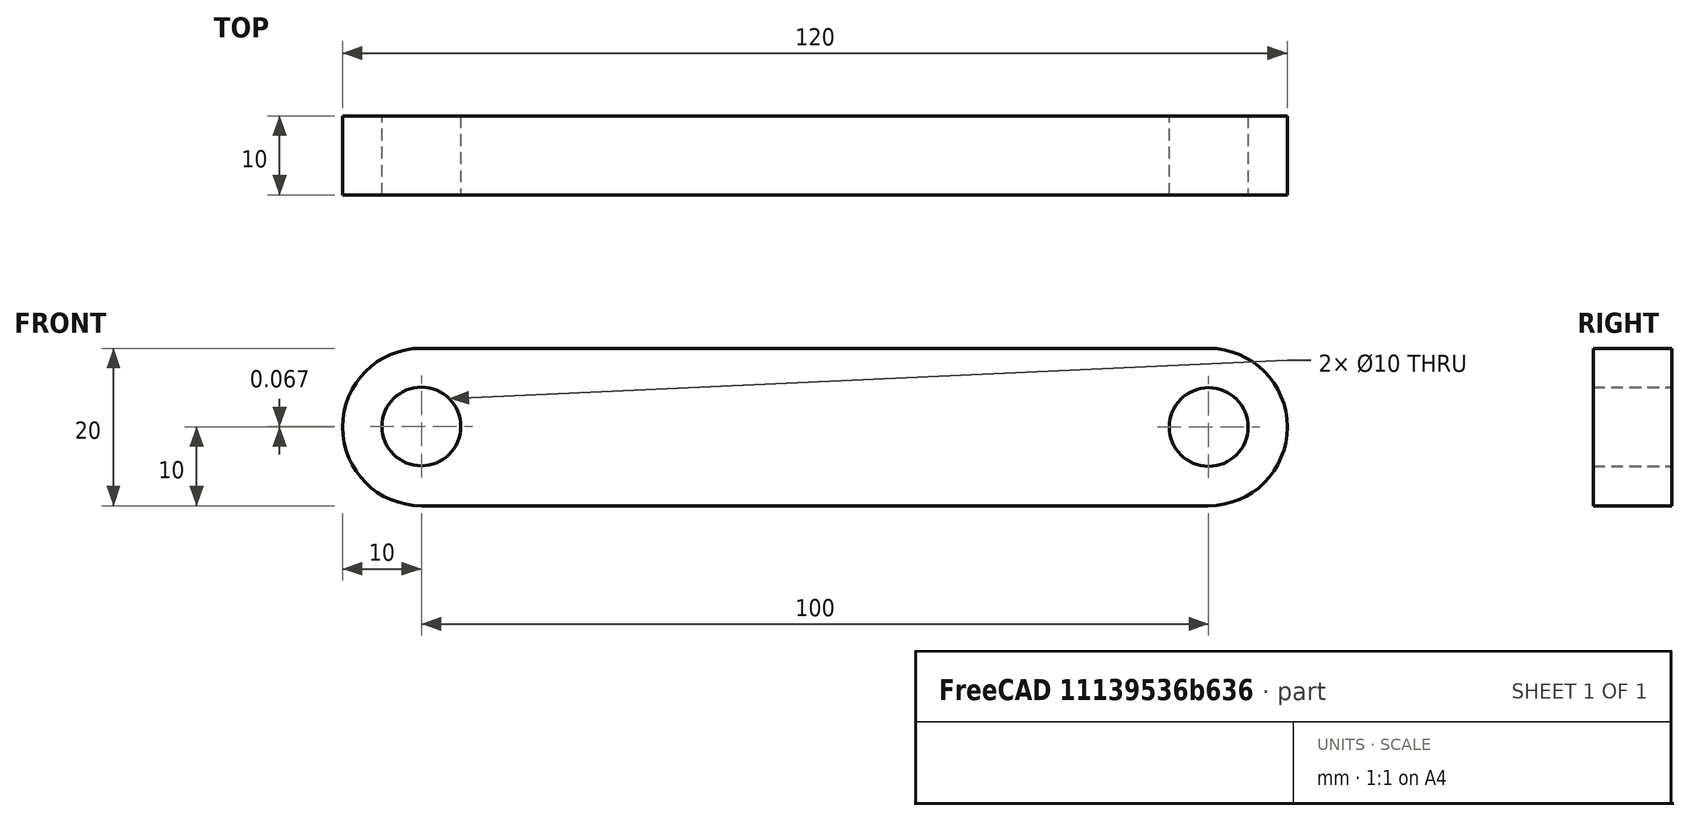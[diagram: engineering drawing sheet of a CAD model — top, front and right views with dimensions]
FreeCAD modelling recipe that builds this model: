
FCSTD DOCUMENT  (FreeCAD 0.21R33668 +26 (Git))
Label: Tuto1-001
License: All rights reserved
LicenseURL: http://en.wikipedia.org/wiki/All_rights_reserved
objects: PartDesign::CoordinateSystem×5, App::DocumentObjectGroup×3, Sketcher::SketchObject×2, App::Link×2, App::FeaturePython×1, App::Part×1, PartDesign::Pad×1, PartDesign::Body×1
note: 10 computed .brp shape members not serialized (recipe doc carries the construction recipe); baked Part::Feature solids carry a one-line shape summary decoded from their .brp

FEATURE [PartDesign::CoordinateSystem] LCS_Origin
  AttacherType = Attacher::AttachEngine3D
  MapMode = 2
  Support = -> [X_Axis]
FEATURE [App::DocumentObjectGroup] Constraints
FEATURE [App::FeaturePython] Variables  # WARN: FeaturePython — macro-defined, semantics opaque (R4)
  Type = App::PropertyContainer
  rotation_bielle1 = 79
FEATURE [App::DocumentObjectGroup] Configurations
FEATURE [Sketcher::SketchObject] Sketch_1
  FullyConstrained = true
  Support = -> [YZ_Plane]
  expr: Constraints[11] = Variables.rotation_bielle1
  sketch-geometry (3):
    g0: LineSegment StartX=90.2102 StartY=121.516 StartZ=0 EndX=1.29856 EndY=242.324 EndZ=0
    g1: LineSegment StartX=0 StartY=120 StartZ=0 EndX=19.0809 EndY=218.163 EndZ=0
    g2: LineSegment StartX=0 StartY=50 StartZ=0 EndX=72.4279 EndY=145.678 EndZ=0
  constraints (12):
    c: PointOnObject(g1,g0)
    c: PointOnObject(g2,g0)
    c: PointOnObject(g1,g-2)
    c: Distance(g1,g0) = 30
    c: Distance(g2,g0) = 30
    c: PointOnObject(g2,g-2)
    c: Distance(g2) = 120
    c: DistanceY(g-1,g1) = 120
    c: Distance(g1,g1) = 100
    c: Distance(g0) = 150
    c: DistanceY(g-1,g2) = 50
    c: Angle(g-1,g1) = 1.37881
FEATURE [PartDesign::CoordinateSystem] LCS_1
  AttacherType = Attacher::AttachEngine3D
  MapMode = 7
  Placement = pos=(0,120,0) rot=(0.990855,-0.095409,-0.095409;1.57998rad)
  Support = -> [Sketch_1]
FEATURE [PartDesign::CoordinateSystem] LCS_2
  AttacherType = Attacher::AttachEngine3D
  MapMode = 7
  Placement = pos=(90.2102,121.516,0) rot=(0.906999,0.297785,0.297785;1.66826rad)
  Support = -> [Sketch_1]
FEATURE [PartDesign::CoordinateSystem] LCS_3
  AttacherType = Attacher::AttachEngine3D
  MapMode = 7
  Placement = pos=(-3.6e-15,50,0) rot=(0.903307,-0.303345,-0.303345;1.67231rad)
  Support = -> [Sketch_1]
FEATURE [PartDesign::CoordinateSystem] LCS_0
  AttacherType = Attacher::AttachEngine3D
  MapMode = 2
  Support = -> [X_Axis001]
FEATURE [App::Link] Body001
  AttachedBy = #LCS_0
  AttachedTo = Parent Assembly#LCS_1
  AttachmentOffset = pos=(0,0,0) rot=(-0.707107,0,0.707107;3.14159rad)
  LinkPlacement = pos=(0,120,0) rot=(-0.651074,-0.536704,0.536704;1.98733rad)
  LinkedObject = -> Body
  Placement = pos=(0,120,0) rot=(-0.651074,-0.536704,0.536704;1.98733rad)
  SolverId = Asm4EE
  expr: Placement = LCS_1.Placement * AttachmentOffset * LCS_0.Placement ^ -1
FEATURE [App::Link] Body002
  AttachedBy = #LCS_0
  AttachedTo = Parent Assembly#LCS_3
  AttachmentOffset = pos=(0,0,0) rot=(-0.707107,0,0.707107;3.14159rad)
  LinkPlacement = pos=(-3.6e-15,50,0) rot=(-0.818014,-0.406727,0.406727;1.77033rad)
  LinkedObject = -> Body
  Placement = pos=(-3.6e-15,50,0) rot=(-0.818014,-0.406727,0.406727;1.77033rad)
  SolverId = Asm4EE
  expr: Placement = LCS_3.Placement * AttachmentOffset * LCS_0.Placement ^ -1
FEATURE [App::Part] Assembly
  AssemblyType = Part::Link
  Group = -> [LCS_Origin,Constraints,Variables,Configurations,Sketch_1,LCS_1,LCS_2,LCS_3,Body001,Body002]
  Origin = -> Origin
  Type = Assembly
FEATURE [Sketcher::SketchObject] Sketch
  FullyConstrained = false
  MapMode = 5
  Placement = pos=(0,0,0) rot=(1,0,0;1.5708rad)
  Support = -> [XZ_Plane001]
  sketch-geometry (6):
    g0: ArcOfCircle CenterX=0 CenterY=0 CenterZ=0 NormalX=0 NormalY=0 NormalZ=1 AngleXU=0 Radius=10 StartAngle=1.5708 EndAngle=4.71239
    g1: ArcOfCircle CenterX=100 CenterY=1.1e-15 CenterZ=0 NormalX=0 NormalY=0 NormalZ=1 AngleXU=0 Radius=10 StartAngle=4.71239 EndAngle=7.85398
    g2: LineSegment StartX=-1.8e-15 StartY=-10 StartZ=0 EndX=100 EndY=-10 EndZ=0
    g3: LineSegment StartX=100 StartY=10 StartZ=0 EndX=7.958e-13 EndY=10 EndZ=0
    g4: Circle CenterX=100 CenterY=1.1e-15 CenterZ=0 NormalX=0 NormalY=0 NormalZ=1 AngleXU=0 Radius=5
    g5: Circle CenterX=0 CenterY=0.067016 CenterZ=0 NormalX=0 NormalY=0 NormalZ=1 AngleXU=0 Radius=5
  constraints (11):
    c: Tangent(g0,g2) = -1.5708
    c: Tangent(g2,g1) = -1.5708
    c: Tangent(g1,g3) = -1.5708
    c: Tangent(g3,g0) = -1.5708
    c: Equal(g0,g1)
    c: Horizontal(g2)
    c: Coincident(g0,g-1)
    c: Coincident(g4,g1)
    c: PointOnObject(g5,g-2)
    c: Radius(g5) = 5
    c: DistanceX(g5,g1) = 100
FEATURE [PartDesign::Pad] Pad
  Direction = (0,-1,-2e-16)
  Length = 10
  Length2 = 10
  Placement = pos=(0,0,0) rot=(1,0,0;1.5708rad)
  Profile = -> Sketch
  ReferenceAxis = -> Sketch [N_Axis]
  Type = 0
FEATURE [PartDesign::Body] Body
  Group = -> [LCS_0,Sketch,Pad]
  Origin = -> Origin001
  Tip = -> Pad
FEATURE [App::DocumentObjectGroup] Parts
  Group = -> [Body]
